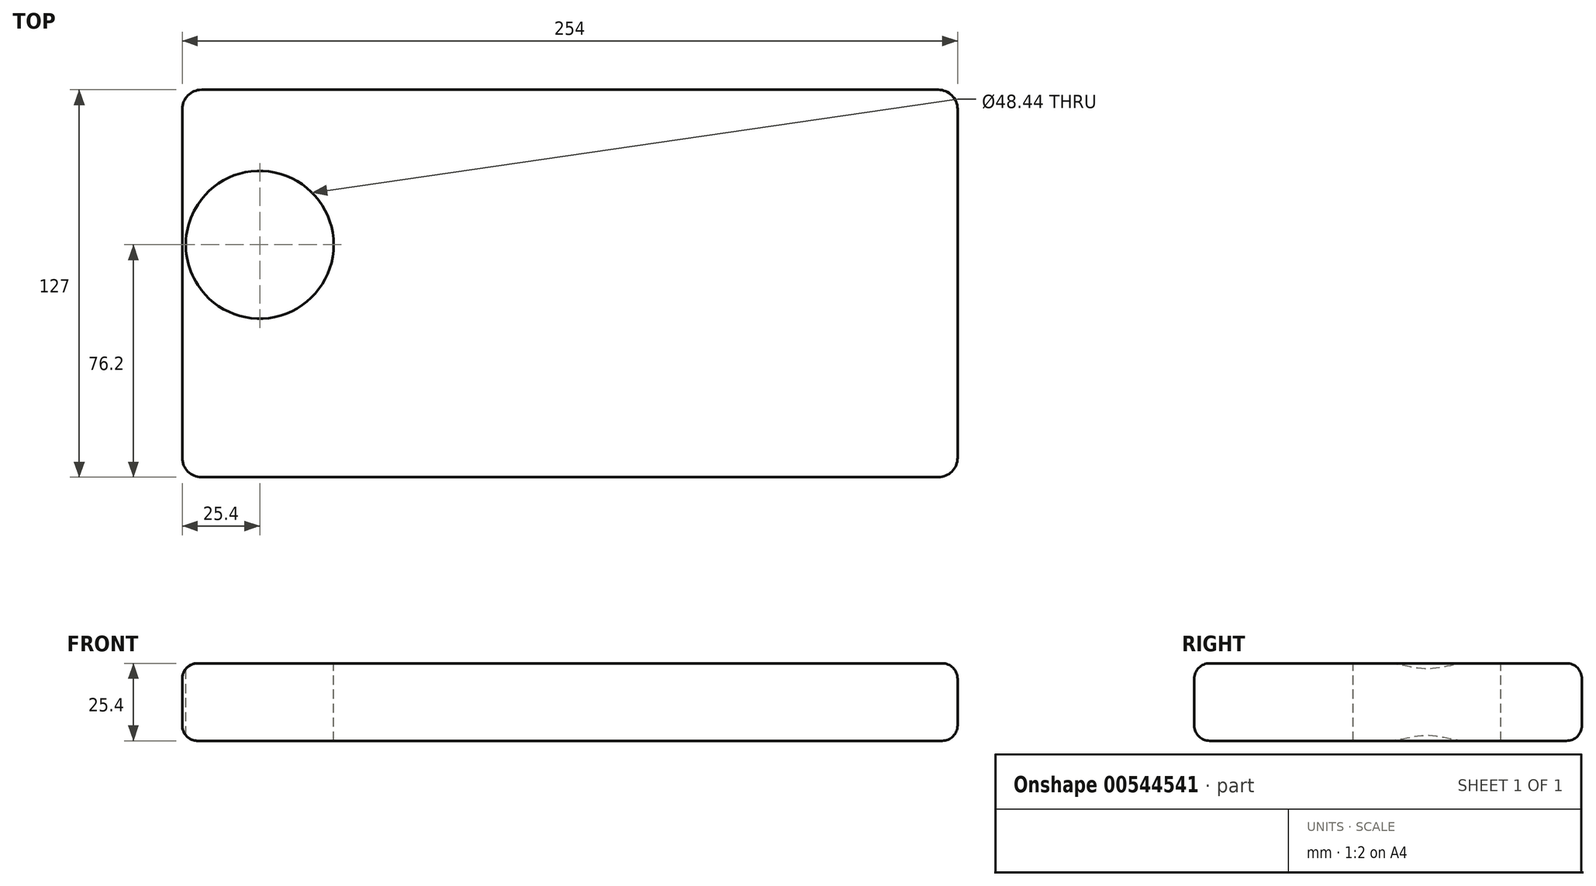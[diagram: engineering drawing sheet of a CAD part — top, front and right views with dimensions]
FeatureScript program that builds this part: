
annotation { "Feature Type Name" : "Feature", "Feature Type Description" : "" }
export const myFeature = defineFeature(function(context is Context, id is Id, definition is map)
    precondition{}
    {
        {
            var Q0;
            Q0=qCreatedBy(makeId("Top.planeOp"),FACE);
            var sketch = newSketch(context, id + "F0", { "sketchPlane" : qUnion([Q0])});
            skLineSegment(sketch, "E0.bottom", {"start": v(-120.65, 63.5) * mm, "end": v(120.65, 63.5) * mm});
            skLineSegment(sketch, "E0.top", {"start": v(-120.65, -63.5) * mm, "end": v(120.65, -63.5) * mm});
            skLineSegment(sketch, "E0.left", {"start": v(-127, 57.15) * mm, "end": v(-127, -57.15) * mm});
            skLineSegment(sketch, "E0.right", {"start": v(127, 57.15) * mm, "end": v(127, -57.15) * mm});
            skPoint(sketch, "E1.visualSharp", {"position": v(-127, 63.5) * mm});
            skArc(sketch, "E1.filletArc", {"start": v(-120.65, 63.5) * mm, "mid": v(-125.14, 61.64) * mm, "end": v(-127, 57.15) * mm});
            skPoint(sketch, "E2.visualSharp", {"position": v(127, 63.5) * mm});
            skArc(sketch, "E2.filletArc", {"start": v(127, 57.15) * mm, "mid": v(125.14, 61.64) * mm, "end": v(120.65, 63.5) * mm});
            skPoint(sketch, "E3.visualSharp", {"position": v(127, -63.5) * mm});
            skArc(sketch, "E3.filletArc", {"start": v(120.65, -63.5) * mm, "mid": v(125.14, -61.64) * mm, "end": v(127, -57.15) * mm});
            skPoint(sketch, "E4.visualSharp", {"position": v(-127, -63.5) * mm});
            skArc(sketch, "E4.filletArc", {"start": v(-127, -57.15) * mm, "mid": v(-125.14, -61.64) * mm, "end": v(-120.65, -63.5) * mm});
            skSolve(sketch);
        }
        {
            var Q0;
            Q0=makeQuery(id+"F0.imprint","IMPRINT",FACE,{"disambiguationData":[TD([[makeQuery(id+"F0.imprint","IMPRINT",EDGE,{"derivedFrom":sQuery(id+"F0.wireOp",EDGE,"E0.bottom")}),-1.0]])]});
            extrude(context, id + "F1", {"entities" : qUnion([Q0]), "depth" : 25.4 * mm, "offsetDistance" : 25.4 * mm});
        }
        {
            var Q0;
            Q0=makeQuery(id+"F1.opExtrude","CAP_FACE",FACE,{"disambiguationData":[OSD([sQuery(id+"F0.wireOp",EDGE,"E0.bottom"),sQuery(id+"F0.wireOp",EDGE,"E0.top"),sQuery(id+"F0.wireOp",EDGE,"E0.left"),sQuery(id+"F0.wireOp",EDGE,"E0.right"),sQuery(id+"F0.wireOp",EDGE,"E1.filletArc"),sQuery(id+"F0.wireOp",EDGE,"E2.filletArc"),sQuery(id+"F0.wireOp",EDGE,"E3.filletArc"),sQuery(id+"F0.wireOp",EDGE,"E4.filletArc")])],"isStart":false});
            var sketch = newSketch(context, id + "F2", { "sketchPlane" : qUnion([Q0])});
            skCircle(sketch, "E5", {"center": v(-101.6, 12.7) * mm, "radius": 24.22 * mm});
            skSolve(sketch);
        }
        {
            var Q0;
            Q0=makeQuery(id+"F2.imprint","IMPRINT",FACE,{"disambiguationData":[TD([[makeQuery(id+"F2.imprint","IMPRINT",EDGE,{"derivedFrom":sQuery(id+"F2.wireOp",EDGE,"E5")}),1.0]])]});
            extrude(context, id + "F3", {"entities" : qUnion([Q0]), "operationType" : NewBodyOperationType.REMOVE, "endBound" : BoundingType.THROUGH_ALL, "oppositeDirection" : true, "depth" : 25.4 * mm, "offsetDistance" : 25.4 * mm});
        }
        {
            var Q0;
            Q0=makeQuery(id+"F1.opExtrude","CAP_EDGE",EDGE,{"disambiguationData":[OSD([sQuery(id+"F0.wireOp",EDGE,"E0.top")])],"isStart":false});
            fillet(context, id + "F4", {"entities" : qUnion([Q0]), "radius" : 5.08 * mm, "tangentPropagation" : true, "allowEdgeOverflow" : false});
        }
        {
            var Q0;
            Q0=makeQuery(id+"F1.opExtrude","CAP_EDGE",EDGE,{"disambiguationData":[OSD([sQuery(id+"F0.wireOp",EDGE,"E0.right")])],"isStart":true});
            fillet(context, id + "F5", {"entities" : qUnion([Q0]), "radius" : 5.08 * mm, "tangentPropagation" : true, "allowEdgeOverflow" : false});
        }
    });
